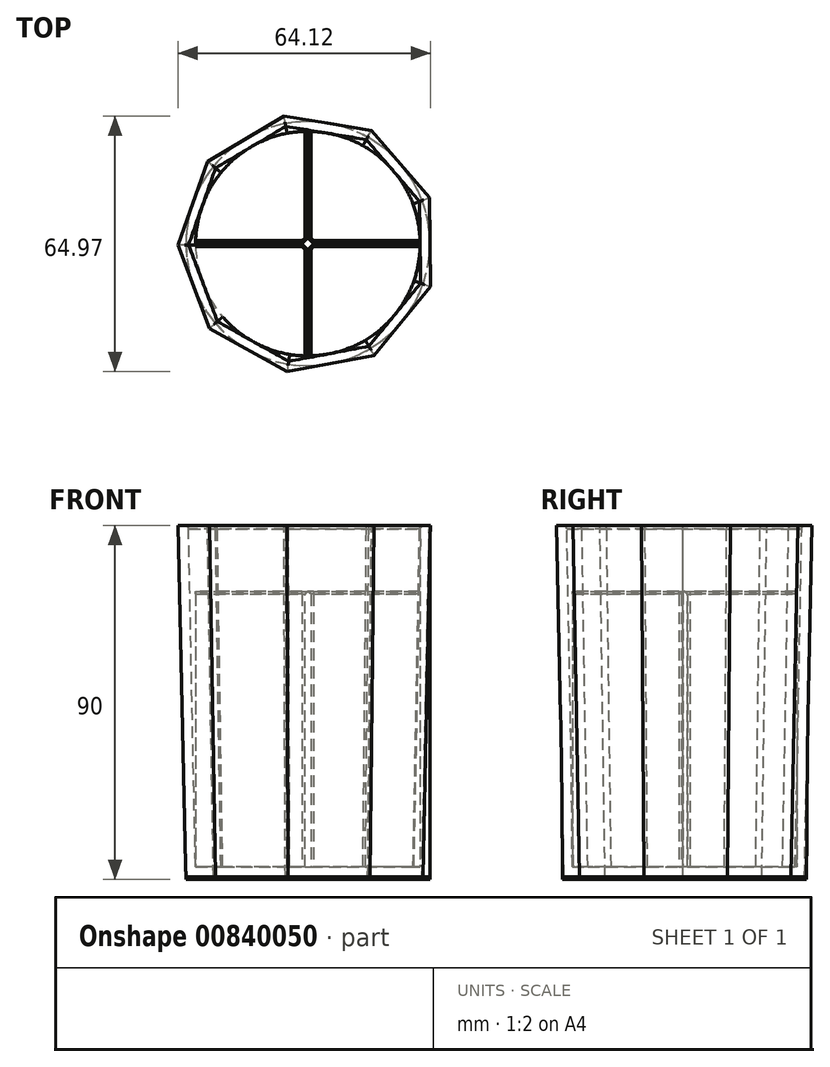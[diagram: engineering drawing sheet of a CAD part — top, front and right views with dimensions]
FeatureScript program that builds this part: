
annotation { "Feature Type Name" : "Feature", "Feature Type Description" : "" }
export const myFeature = defineFeature(function(context is Context, id is Id, definition is map)
    precondition{}
    {
        {
            var Q0;
            Q0=qCreatedBy(makeId("Top.planeOp"),FACE);
            var sketch = newSketch(context, id + "F0", { "sketchPlane" : qUnion([Q0])});
            skCircle(sketch, "E0", {"center": v(0, 0) * mm, "radius": 31 * mm});
            skSolve(sketch);
        }
        {
            var Q0;
            Q0=makeQuery(id+"F0.imprint","IMPRINT",FACE,{"disambiguationData":[TD([[makeQuery(id+"F0.imprint","IMPRINT",EDGE,{"derivedFrom":sQuery(id+"F0.wireOp",EDGE,"E0")}),1.0]])]});
            extrude(context, id + "F1", {"entities" : qUnion([Q0]), "depth" : 0.7 * mm, "offsetDistance" : 25 * mm});
        }
        {
            var Q0;
            Q0=makeQuery(id+"F1.opExtrude","CAP_FACE",FACE,{"disambiguationData":[OSD([sQuery(id+"F0.wireOp",EDGE,"E0")])],"isStart":false});
            var sketch = newSketch(context, id + "F2", { "sketchPlane" : qUnion([Q0])});
            skSolve(sketch);
        }
        {
            var Q0;
            Q0=qCreatedBy(makeId("Top.planeOp"),FACE);
            var Q1;
            Q1 = qBodyType(qCreatedBy(id + "F4" ,EDGE), BodyType.WIRE);
            cPlane(context, id + "F3", {"entities" : qUnion([Q0, Q1]), "cplaneType" : CPlaneType.OFFSET, "offset" : 90 * mm, "width" : 150 * mm, "height" : 150 * mm});
        }
        {
            var Q0;
            Q0=qCreatedBy(id+"F3.planeOp",FACE);
            var sketch = newSketch(context, id + "F4", { "sketchPlane" : qUnion([Q0])});
            skCircle(sketch, "E1.cCircle", {"center": v(0, 0) * mm, "radius": 31 * mm, "construction": true});
            skLineSegment(sketch, "E1.0", {"start": v(30.86, 11.65) * mm, "end": v(31.13, -10.9) * mm});
            skLineSegment(sketch, "E1.1", {"start": v(31.13, -10.9) * mm, "end": v(16.84, -28.37) * mm});
            skLineSegment(sketch, "E1.2", {"start": v(16.84, -28.37) * mm, "end": v(-5.34, -32.55) * mm});
            skLineSegment(sketch, "E1.3", {"start": v(-5.34, -32.55) * mm, "end": v(-25.01, -21.5) * mm});
            skLineSegment(sketch, "E1.4", {"start": v(-25.01, -21.5) * mm, "end": v(-32.99, -0.4) * mm});
            skLineSegment(sketch, "E1.5", {"start": v(-32.99, -0.4) * mm, "end": v(-25.52, 20.9) * mm});
            skLineSegment(sketch, "E1.6", {"start": v(-25.52, 20.9) * mm, "end": v(-6.12, 32.42) * mm});
            skLineSegment(sketch, "E1.7", {"start": v(-6.12, 32.42) * mm, "end": v(16.15, 28.77) * mm});
            skLineSegment(sketch, "E1.8", {"start": v(16.15, 28.77) * mm, "end": v(30.86, 11.65) * mm});
            skPoint(sketch, "E1.0.midPoint", {"position": v(31, 0.37) * mm});
            skSolve(sketch);
        }
        {
            var Q0;
            Q0=makeQuery(id+"F2.imprint","IMPRINT",FACE,{"disambiguationData":[TD([[makeQuery(id+"F2.imprint","IMPRINT",EDGE,{"derivedFrom":makeQuery(id+"F1.opExtrude","CAP_EDGE",EDGE,{"disambiguationData":[OSD([sQuery(id+"F0.wireOp",EDGE,"E0")])],"isStart":false})}),1.0]])]});
            var Q1;
            Q1=makeQuery(id+"F4.imprint","IMPRINT",FACE,{"disambiguationData":[TD([[makeQuery(id+"F4.imprint","IMPRINT",EDGE,{"derivedFrom":sQuery(id+"F4.wireOp",EDGE,"E1.0")}),-1.0]])]});
            loft(context, id + "F5", {"sheetProfilesArray" : [{ "sheetProfileEntities" : qUnion([Q0]) }, { "sheetProfileEntities" : qUnion([Q1]) }]});
        }
        {
            var Q0;
            Q0=makeQuery(id+"F5.opLoft","CAP_FACE",FACE,{"disambiguationData":[OSD([makeQuery(id+"F4.imprint","IMPRINT",FACE,{"disambiguationData":[TD([[makeQuery(id+"F4.imprint","IMPRINT",EDGE,{"derivedFrom":sQuery(id+"F4.wireOp",EDGE,"E1.0")}),-1.0]])]})])],"isStart":true});
            shell(context, id + "F6", {"entities" : qUnion([Q0]), "thickness" : 2.5 * mm});
        }
        {
            var Q0;
            Q0=makeQuery(id+"F6.opShell","OFFSET_FACE",FACE,{"disambiguationData":[OSD([makeQuery(id+"F2.imprint","IMPRINT",FACE,{"disambiguationData":[TD([[makeQuery(id+"F2.imprint","IMPRINT",EDGE,{"derivedFrom":makeQuery(id+"F1.opExtrude","CAP_EDGE",EDGE,{"disambiguationData":[OSD([sQuery(id+"F0.wireOp",EDGE,"E0")])],"isStart":false})}),1.0]])]})])]});
            var sketch = newSketch(context, id + "F7", { "sketchPlane" : qUnion([Q0])});
            skLineSegment(sketch, "E2.bottom", {"start": v(30.5, -0.75) * mm, "end": v(-30.5, -0.75) * mm});
            skLineSegment(sketch, "E2.top", {"start": v(30.5, 0.75) * mm, "end": v(-30.5, 0.75) * mm});
            skLineSegment(sketch, "E2.left", {"start": v(30.5, -0.75) * mm, "end": v(30.5, 0.75) * mm});
            skLineSegment(sketch, "E2.right", {"start": v(-30.5, -0.75) * mm, "end": v(-30.5, 0.75) * mm});
            skPoint(sketch, "E2.middle", {"position": v(0, 0) * mm});
            skLineSegment(sketch, "E3.bottom", {"start": v(-0.75, 37.5) * mm, "end": v(0.75, 37.5) * mm});
            skLineSegment(sketch, "E3.top", {"start": v(-0.75, -37.5) * mm, "end": v(0.75, -37.5) * mm});
            skLineSegment(sketch, "E3.left", {"start": v(-0.75, 37.5) * mm, "end": v(-0.75, -37.5) * mm});
            skLineSegment(sketch, "E3.right", {"start": v(0.75, 37.5) * mm, "end": v(0.75, -37.5) * mm});
            skSolve(sketch);
        }
        {
            var Q0;
            Q0=makeQuery(id+"F6.opShell","OFFSET_EDGE",EDGE,{"disambiguationData":[OSD([sQuery(id+"F4.wireOp",EDGE,"E1.0"),sQuery(id+"F4.wireOp",EDGE,"E1.1"),sQuery(id+"F4.wireOp",EDGE,"E1.2")])]});
            var Q1;
            Q1=makeQuery(id+"F6.opShell","OFFSET_EDGE",EDGE,{"disambiguationData":[OSD([sQuery(id+"F4.wireOp",EDGE,"E1.1"),sQuery(id+"F4.wireOp",EDGE,"E1.2"),sQuery(id+"F4.wireOp",EDGE,"E1.3")])]});
            var Q2;
            Q2=makeQuery(id+"F6.opShell","OFFSET_EDGE",EDGE,{"disambiguationData":[OSD([sQuery(id+"F4.wireOp",EDGE,"E1.2"),sQuery(id+"F4.wireOp",EDGE,"E1.3"),sQuery(id+"F4.wireOp",EDGE,"E1.4")])]});
            var Q3;
            Q3=makeQuery(id+"F6.opShell","OFFSET_EDGE",EDGE,{"disambiguationData":[OSD([sQuery(id+"F4.wireOp",EDGE,"E1.3"),sQuery(id+"F4.wireOp",EDGE,"E1.4"),sQuery(id+"F4.wireOp",EDGE,"E1.5")])]});
            var Q4;
            Q4=makeQuery(id+"F6.opShell","OFFSET_EDGE",EDGE,{"disambiguationData":[OSD([sQuery(id+"F4.wireOp",EDGE,"E1.4"),sQuery(id+"F4.wireOp",EDGE,"E1.5"),sQuery(id+"F4.wireOp",EDGE,"E1.6")])]});
            var Q5;
            Q5=makeQuery(id+"F6.opShell","OFFSET_EDGE",EDGE,{"disambiguationData":[OSD([sQuery(id+"F4.wireOp",EDGE,"E1.5"),sQuery(id+"F4.wireOp",EDGE,"E1.6"),sQuery(id+"F4.wireOp",EDGE,"E1.7")])]});
            var Q6;
            Q6=makeQuery(id+"F6.opShell","OFFSET_EDGE",EDGE,{"disambiguationData":[OSD([sQuery(id+"F4.wireOp",EDGE,"E1.6"),sQuery(id+"F4.wireOp",EDGE,"E1.7"),sQuery(id+"F4.wireOp",EDGE,"E1.8")])]});
            var Q7;
            Q7=makeQuery(id+"F6.opShell","OFFSET_EDGE",EDGE,{"disambiguationData":[OSD([sQuery(id+"F4.wireOp",EDGE,"E1.0"),sQuery(id+"F4.wireOp",EDGE,"E1.7"),sQuery(id+"F4.wireOp",EDGE,"E1.8")])]});
            var Q8;
            Q8=makeQuery(id+"F6.opShell","OFFSET_EDGE",EDGE,{"disambiguationData":[OSD([sQuery(id+"F4.wireOp",EDGE,"E1.0"),sQuery(id+"F4.wireOp",EDGE,"E1.1"),sQuery(id+"F4.wireOp",EDGE,"E1.8")])]});
            fillet(context, id + "F8", {"entities" : qUnion([Q0, Q1, Q2, Q3, Q4, Q5, Q6, Q7, Q8]), "radius" : 1 * mm, "tangentPropagation" : true, "allowEdgeOverflow" : false});
        }
        {
            var Q0;
            {var subQ0=sQuery(id+"F7.wireOp",EDGE,"E3.right");var subQ1=sQuery(id+"F7.wireOp",EDGE,"E2.top");var subQ2=makeQuery(id+"F7.imprint","INTERSECT",VERTEX,{"derivedFrom":[subQ1,subQ0]});Q0=makeQuery(id+"F7.imprint","IMPRINT",FACE,{"disambiguationData":[TD([[makeQuery(id+"F7.imprint","IMPRINT",EDGE,{"disambiguationData":[TD([[subQ2,-1.0]])],"derivedFrom":subQ1}),-1.0]])]});}
            var Q1;
            {var subQ0=sQuery(id+"F7.wireOp",EDGE,"E3.left");var subQ1=sQuery(id+"F7.wireOp",EDGE,"E2.bottom");var subQ2=makeQuery(id+"F7.imprint","INTERSECT",VERTEX,{"derivedFrom":[subQ1,subQ0]});Q1=makeQuery(id+"F7.imprint","IMPRINT",FACE,{"disambiguationData":[TD([[makeQuery(id+"F7.imprint","IMPRINT",EDGE,{"disambiguationData":[TD([[subQ2,1.0]])],"derivedFrom":subQ0}),-1.0]])]});}
            var Q2;
            {var subQ0=sQuery(id+"F7.wireOp",EDGE,"E3.right");var subQ1=sQuery(id+"F7.wireOp",EDGE,"E2.bottom");var subQ2=makeQuery(id+"F7.imprint","INTERSECT",VERTEX,{"derivedFrom":[subQ1,subQ0]});Q2=makeQuery(id+"F7.imprint","IMPRINT",FACE,{"disambiguationData":[TD([[makeQuery(id+"F7.imprint","IMPRINT",EDGE,{"disambiguationData":[TD([[subQ2,-1.0]])],"derivedFrom":subQ1}),-1.0]])]});}
            var Q3;
            {var subQ0=sQuery(id+"F7.wireOp",EDGE,"E3.right");var subQ1=sQuery(id+"F7.wireOp",EDGE,"E2.bottom");var subQ2=makeQuery(id+"F7.imprint","INTERSECT",VERTEX,{"derivedFrom":[subQ1,subQ0]});Q3=makeQuery(id+"F7.imprint","IMPRINT",FACE,{"disambiguationData":[TD([[makeQuery(id+"F7.imprint","IMPRINT",EDGE,{"disambiguationData":[TD([[subQ2,-1.0]])],"derivedFrom":subQ1}),1.0]])]});}
            var Q4;
            {var subQ0=sQuery(id+"F7.wireOp",EDGE,"E3.right");var subQ1=sQuery(id+"F7.wireOp",EDGE,"E2.bottom");var subQ2=makeQuery(id+"F7.imprint","INTERSECT",VERTEX,{"derivedFrom":[subQ1,subQ0]});Q4=makeQuery(id+"F7.imprint","IMPRINT",FACE,{"disambiguationData":[TD([[makeQuery(id+"F7.imprint","IMPRINT",EDGE,{"disambiguationData":[TD([[subQ2,1.0]])],"derivedFrom":subQ0}),1.0]])]});}
            var Q5;
            {var subQ0=sQuery(id+"F7.wireOp",EDGE,"E2.left");Q5=makeQuery(id+"F7.imprint","IMPRINT",FACE,{"disambiguationData":[TD([[makeQuery(id+"F7.imprint","IMPRINT",EDGE,{"derivedFrom":subQ0}),1.0]])]});}
            extrude(context, id + "F9", {"entities" : qUnion([Q0, Q1, Q2, Q3, Q4, Q5]), "operationType" : NewBodyOperationType.ADD, "depth" : 70 * mm, "offsetDistance" : 25 * mm});
        }
        {
            var Q0;
            {var subQ0=sQuery(id+"F7.wireOp",EDGE,"E3.right");Q0=makeQuery(id+"F9.opExtrude","CAP_EDGE",EDGE,{"disambiguationData":[OSD([subQ0]),TDD([makeQuery(id+"F7.imprint","IMPRINT",EDGE,{"disambiguationData":[TD([[makeQuery(id+"F7.imprint","INTERSECT",VERTEX,{"derivedFrom":[sQuery(id+"F7.wireOp",EDGE,"E2.top"),subQ0]}),1.0]])],"derivedFrom":subQ0})])],"isStart":false});}
            var Q1;
            {var subQ0=sQuery(id+"F7.wireOp",EDGE,"E2.top");Q1=makeQuery(id+"F9.opExtrude","CAP_EDGE",EDGE,{"disambiguationData":[OSD([subQ0]),TDD([makeQuery(id+"F7.imprint","IMPRINT",EDGE,{"disambiguationData":[TD([[makeQuery(id+"F7.imprint","INTERSECT",VERTEX,{"derivedFrom":[subQ0,sQuery(id+"F7.wireOp",EDGE,"E2.left")]}),-1.0]])],"derivedFrom":subQ0}),makeQuery(id+"F7.imprint","IMPRINT",EDGE,{"disambiguationData":[TD([[makeQuery(id+"F7.imprint","INTERSECT",VERTEX,{"derivedFrom":[subQ0,sQuery(id+"F7.wireOp",EDGE,"E3.right")]}),1.0]])],"derivedFrom":subQ0})])],"isStart":false});}
            var Q2;
            {var subQ0=sQuery(id+"F7.wireOp",EDGE,"E2.bottom");Q2=makeQuery(id+"F9.opExtrude","CAP_EDGE",EDGE,{"disambiguationData":[OSD([subQ0]),TDD([makeQuery(id+"F7.imprint","IMPRINT",EDGE,{"disambiguationData":[TD([[makeQuery(id+"F7.imprint","INTERSECT",VERTEX,{"derivedFrom":[subQ0,sQuery(id+"F7.wireOp",EDGE,"E2.left")]}),-1.0]])],"derivedFrom":subQ0}),makeQuery(id+"F7.imprint","IMPRINT",EDGE,{"disambiguationData":[TD([[makeQuery(id+"F7.imprint","INTERSECT",VERTEX,{"derivedFrom":[subQ0,sQuery(id+"F7.wireOp",EDGE,"E3.right")]}),1.0]])],"derivedFrom":subQ0})])],"isStart":false});}
            var Q3;
            {var subQ0=sQuery(id+"F7.wireOp",EDGE,"E3.right");Q3=makeQuery(id+"F9.opExtrude","CAP_EDGE",EDGE,{"disambiguationData":[OSD([subQ0]),TDD([makeQuery(id+"F7.imprint","IMPRINT",EDGE,{"disambiguationData":[TD([[makeQuery(id+"F7.imprint","INTERSECT",VERTEX,{"derivedFrom":[sQuery(id+"F7.wireOp",EDGE,"E2.bottom"),subQ0]}),-1.0]])],"derivedFrom":subQ0})])],"isStart":false});}
            var Q4;
            {var subQ0=sQuery(id+"F7.wireOp",EDGE,"E3.left");Q4=makeQuery(id+"F9.opExtrude","CAP_EDGE",EDGE,{"disambiguationData":[OSD([subQ0]),TDD([makeQuery(id+"F7.imprint","IMPRINT",EDGE,{"disambiguationData":[TD([[makeQuery(id+"F7.imprint","INTERSECT",VERTEX,{"derivedFrom":[sQuery(id+"F7.wireOp",EDGE,"E2.bottom"),subQ0]}),-1.0]])],"derivedFrom":subQ0})])],"isStart":false});}
            var Q5;
            {var subQ0=sQuery(id+"F7.wireOp",EDGE,"E2.bottom");Q5=makeQuery(id+"F9.opExtrude","CAP_EDGE",EDGE,{"disambiguationData":[OSD([subQ0]),TDD([makeQuery(id+"F7.imprint","IMPRINT",EDGE,{"disambiguationData":[TD([[makeQuery(id+"F7.imprint","INTERSECT",VERTEX,{"derivedFrom":[subQ0,sQuery(id+"F7.wireOp",EDGE,"E3.left")]}),-1.0]])],"derivedFrom":subQ0})])],"isStart":false});}
            var Q6;
            {var subQ0=sQuery(id+"F7.wireOp",EDGE,"E2.top");Q6=makeQuery(id+"F9.opExtrude","CAP_EDGE",EDGE,{"disambiguationData":[OSD([subQ0]),TDD([makeQuery(id+"F7.imprint","IMPRINT",EDGE,{"disambiguationData":[TD([[makeQuery(id+"F7.imprint","INTERSECT",VERTEX,{"derivedFrom":[subQ0,sQuery(id+"F7.wireOp",EDGE,"E3.left")]}),-1.0]])],"derivedFrom":subQ0})])],"isStart":false});}
            var Q7;
            Q7=makeQuery(id+"F9.opExtrude","SWEPT_EDGE",EDGE,{"disambiguationData":[OSD([sQuery(id+"F7.wireOp",EDGE,"E2.bottom"),sQuery(id+"F7.wireOp",EDGE,"E3.right")])]});
            var Q8;
            Q8=makeQuery(id+"F9.opExtrude","SWEPT_EDGE",EDGE,{"disambiguationData":[OSD([sQuery(id+"F7.wireOp",EDGE,"E2.top"),sQuery(id+"F7.wireOp",EDGE,"E3.right")])]});
            var Q9;
            Q9=makeQuery(id+"F9.opExtrude","SWEPT_EDGE",EDGE,{"disambiguationData":[OSD([sQuery(id+"F7.wireOp",EDGE,"E2.bottom"),sQuery(id+"F7.wireOp",EDGE,"E3.left")])]});
            var Q10;
            Q10=makeQuery(id+"F9.opExtrude","SWEPT_EDGE",EDGE,{"disambiguationData":[OSD([sQuery(id+"F7.wireOp",EDGE,"E2.top"),sQuery(id+"F7.wireOp",EDGE,"E3.left")])]});
            var Q11;
            {var subQ0=sQuery(id+"F7.wireOp",EDGE,"E3.left");Q11=makeQuery(id+"F9.opExtrude","CAP_EDGE",EDGE,{"disambiguationData":[OSD([subQ0]),TDD([makeQuery(id+"F7.imprint","IMPRINT",EDGE,{"disambiguationData":[TD([[makeQuery(id+"F7.imprint","INTERSECT",VERTEX,{"derivedFrom":[sQuery(id+"F7.wireOp",EDGE,"E2.top"),subQ0]}),1.0]])],"derivedFrom":subQ0})])],"isStart":false});}
            chamfer(context, id + "F10", {"entities" : qUnion([Q0, Q1, Q2, Q3, Q4, Q5, Q6, Q7, Q8, Q9, Q10, Q11]), "width" : 0.7 * mm, "tangentPropagation" : true});
        }
    });
